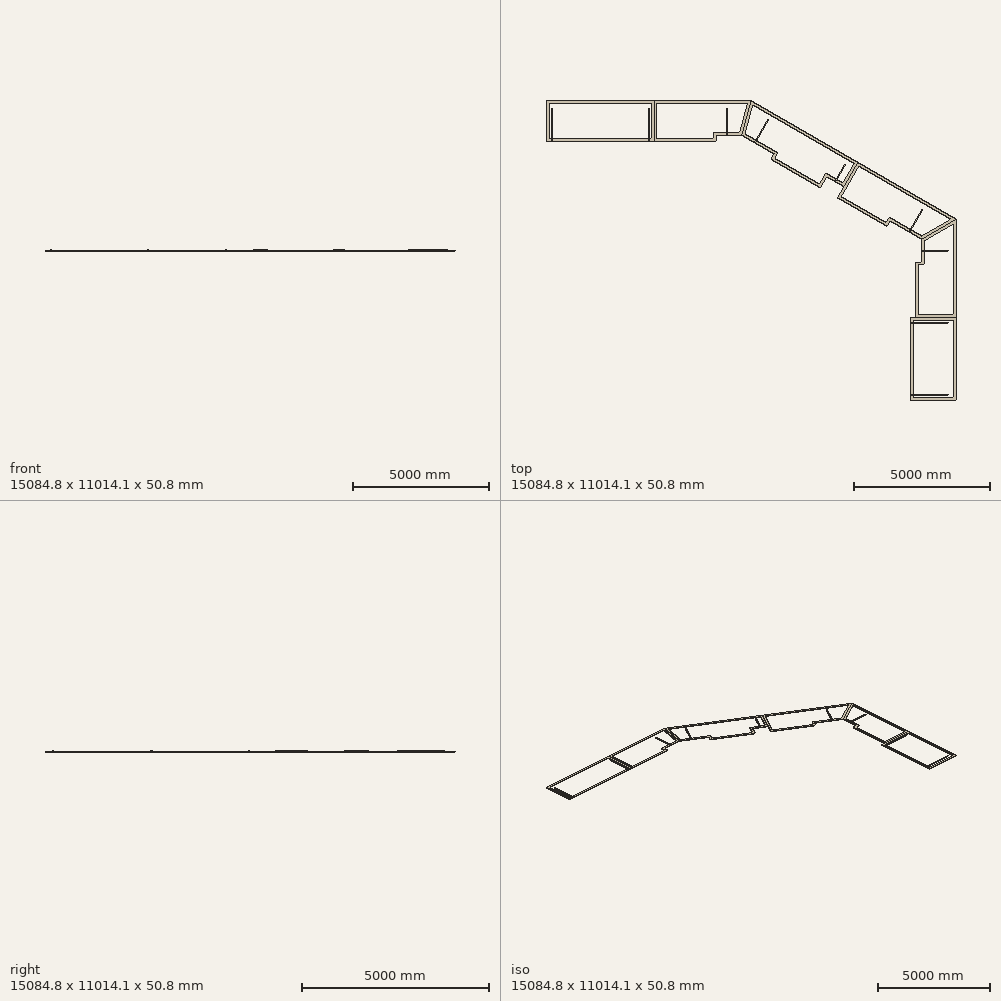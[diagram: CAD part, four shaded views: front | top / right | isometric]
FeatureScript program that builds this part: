
annotation { "Feature Type Name" : "Feature", "Feature Type Description" : "" }
export const myFeature = defineFeature(function(context is Context, id is Id, definition is map)
    precondition{}
    {
        {
            var Q0;
            Q0=qCreatedBy(makeId("Top.planeOp"),FACE);
            var sketch = newSketch(context, id + "F0", { "sketchPlane" : qUnion([Q0])});
            skLineSegment(sketch, "E0", {"start": v(0, 0) * mm, "end": v(7528.5, 0) * mm});
            skLineSegment(sketch, "E1", {"start": v(7528.5, 0) * mm, "end": v(15084.8, -4362.64) * mm});
            skLineSegment(sketch, "E2", {"start": v(15084.8, -4362.64) * mm, "end": v(15084.8, -11014.07) * mm});
            skLineSegment(sketch, "E3", {"start": v(15084.8, -11014.07) * mm, "end": v(13383, -11014.07) * mm});
            skLineSegment(sketch, "E4", {"start": v(13383, -11014.07) * mm, "end": v(13383, -7966.07) * mm});
            skLineSegment(sketch, "E5", {"start": v(13383, -7966.07) * mm, "end": v(13586.2, -7966.07) * mm});
            skLineSegment(sketch, "E6", {"start": v(13586.2, -7966.07) * mm, "end": v(13586.2, -5934.07) * mm});
            skLineSegment(sketch, "E7", {"start": v(13586.2, -5934.07) * mm, "end": v(13814.8, -5934.07) * mm});
            skLineSegment(sketch, "E8", {"start": v(13814.8, -5934.07) * mm, "end": v(13814.8, -5095.87) * mm});
            skLineSegment(sketch, "E9", {"start": v(13814.8, -5095.87) * mm, "end": v(12654.47, -4425.95) * mm});
            skLineSegment(sketch, "E10", {"start": v(12654.47, -4425.95) * mm, "end": v(12540.17, -4623.92) * mm});
            skLineSegment(sketch, "E11", {"start": v(12540.17, -4623.92) * mm, "end": v(10714.41, -3569.82) * mm});
            skLineSegment(sketch, "E12", {"start": v(10714.41, -3569.82) * mm, "end": v(10949.36, -3162.88) * mm});
            skLineSegment(sketch, "E13", {"start": v(10949.36, -3162.88) * mm, "end": v(10322.45, -2800.93) * mm});
            skLineSegment(sketch, "E14", {"start": v(10322.45, -2800.93) * mm, "end": v(10087.5, -3207.87) * mm});
            skLineSegment(sketch, "E15", {"start": v(10087.5, -3207.87) * mm, "end": v(8261.74, -2153.77) * mm});
            skLineSegment(sketch, "E16", {"start": v(8261.74, -2153.77) * mm, "end": v(8376.04, -1955.8) * mm});
            skLineSegment(sketch, "E17", {"start": v(8376.04, -1955.8) * mm, "end": v(7188.2, -1270) * mm});
            skLineSegment(sketch, "E18", {"start": v(7188.2, -1270) * mm, "end": v(6248.4, -1270) * mm});
            skLineSegment(sketch, "E19", {"start": v(6248.4, -1270) * mm, "end": v(6248.4, -1498.6) * mm});
            skLineSegment(sketch, "E20", {"start": v(6248.4, -1498.6) * mm, "end": v(0, -1498.6) * mm});
            skLineSegment(sketch, "E21", {"start": v(0, -1498.6) * mm, "end": v(0, 0) * mm});
            skLineSegment(sketch, "E22", {"start": v(3962.4, 0) * mm, "end": v(3962.4, -1498.6) * mm});
            skLineSegment(sketch, "E23", {"start": v(10949.36, -3162.88) * mm, "end": v(11463.71, -2272) * mm});
            skLineSegment(sketch, "E24", {"start": v(13586.2, -7966.07) * mm, "end": v(15084.8, -7966.07) * mm});
            skLineSegment(sketch, "E25", {"start": v(7188.2, -1270) * mm, "end": v(7528.5, 0) * mm});
            skLineSegment(sketch, "E26", {"start": v(13814.8, -5095.87) * mm, "end": v(15084.8, -4362.64) * mm});
            skLineSegment(sketch, "E27.0", {"start": v(6146.8, -1397) * mm, "end": v(4064, -1397) * mm});
            skLineSegment(sketch, "E27.1", {"start": v(6146.8, -1168.4) * mm, "end": v(6146.8, -1397) * mm});
            skLineSegment(sketch, "E27.2", {"start": v(7110.24, -1168.4) * mm, "end": v(6146.8, -1168.4) * mm});
            skLineSegment(sketch, "E27.3", {"start": v(8514.83, -1918.61) * mm, "end": v(7306.52, -1221) * mm});
            skLineSegment(sketch, "E27.4", {"start": v(8400.53, -2116.59) * mm, "end": v(8514.83, -1918.61) * mm});
            skLineSegment(sketch, "E27.5", {"start": v(101.6, -1397) * mm, "end": v(101.6, -101.6) * mm});
            skLineSegment(sketch, "E27.6", {"start": v(10050.3, -3069.09) * mm, "end": v(8400.53, -2116.59) * mm});
            skLineSegment(sketch, "E27.7", {"start": v(10285.26, -2662.14) * mm, "end": v(10050.3, -3069.09) * mm});
            skLineSegment(sketch, "E27.9", {"start": v(10853.2, -3532.64) * mm, "end": v(11049.76, -3192.19) * mm});
            skLineSegment(sketch, "E27.10", {"start": v(12502.98, -4485.14) * mm, "end": v(10853.2, -3532.64) * mm});
            skLineSegment(sketch, "E27.11", {"start": v(12617.28, -4287.16) * mm, "end": v(12502.98, -4485.14) * mm});
            skLineSegment(sketch, "E27.12", {"start": v(14983.2, -10912.47) * mm, "end": v(13484.6, -10912.47) * mm});
            skLineSegment(sketch, "E27.13", {"start": v(14983.2, -4538.62) * mm, "end": v(14983.2, -7864.47) * mm});
            skLineSegment(sketch, "E27.14", {"start": v(7501.27, -101.6) * mm, "end": v(7501.27, -101.6) * mm});
            skLineSegment(sketch, "E27.15", {"start": v(101.6, -101.6) * mm, "end": v(3860.8, -101.6) * mm});
            skLineSegment(sketch, "E27.16", {"start": v(13484.6, -10912.47) * mm, "end": v(13484.6, -8067.67) * mm});
            skLineSegment(sketch, "E27.17", {"start": v(13484.6, -8067.67) * mm, "end": v(13531.47, -8067.67) * mm});
            skLineSegment(sketch, "E27.19", {"start": v(13687.8, -6035.67) * mm, "end": v(13916.4, -6035.67) * mm});
            skLineSegment(sketch, "E27.20", {"start": v(13916.4, -6035.67) * mm, "end": v(13916.4, -5154.53) * mm});
            skLineSegment(sketch, "E27.21", {"start": v(13814.8, -4978.56) * mm, "end": v(12617.28, -4287.16) * mm});
            skLineSegment(sketch, "E28.0", {"start": v(3860.8, -101.6) * mm, "end": v(3860.8, -1397) * mm});
            skLineSegment(sketch, "E29.0", {"start": v(4064, -101.6) * mm, "end": v(4064, -1397) * mm});
            skLineSegment(sketch, "E30.0", {"start": v(7306.52, -1221) * mm, "end": v(7592.36, -154.2) * mm});
            skLineSegment(sketch, "E31.0", {"start": v(7110.24, -1168.4) * mm, "end": v(7396.09, -101.6) * mm});
            skLineSegment(sketch, "E32.trimOffspring", {"start": v(4064, -101.6) * mm, "end": v(7396.09, -101.6) * mm});
            skLineSegment(sketch, "E33.trimOffspring", {"start": v(3860.8, -1397) * mm, "end": v(101.6, -1397) * mm});
            skLineSegment(sketch, "E34.trimOffspring", {"start": v(7592.36, -154.2) * mm, "end": v(11324.92, -2309.19) * mm});
            skLineSegment(sketch, "E35.trimOffspring", {"start": v(7215.42, -1168.4) * mm, "end": v(7215.42, -1168.4) * mm});
            skLineSegment(sketch, "E36.0", {"start": v(10998.96, -3280.18) * mm, "end": v(11500.9, -2410.79) * mm});
            skLineSegment(sketch, "E37.0", {"start": v(10912.17, -3024.09) * mm, "end": v(11324.92, -2309.19) * mm});
            skLineSegment(sketch, "E38.0", {"start": v(13916.4, -5154.53) * mm, "end": v(14983.2, -4538.62) * mm});
            skLineSegment(sketch, "E39.0", {"start": v(13814.8, -4978.56) * mm, "end": v(14881.6, -4362.64) * mm});
            skLineSegment(sketch, "E40.0", {"start": v(13429.87, -8067.67) * mm, "end": v(14983.2, -8067.67) * mm});
            skLineSegment(sketch, "E41.0", {"start": v(13687.8, -7864.47) * mm, "end": v(14983.2, -7864.47) * mm});
            skLineSegment(sketch, "E42.trimOffspring", {"start": v(10912.17, -3024.09) * mm, "end": v(10285.26, -2662.14) * mm});
            skLineSegment(sketch, "E43.trimOffspring", {"start": v(11500.9, -2410.79) * mm, "end": v(14881.6, -4362.64) * mm});
            skLineSegment(sketch, "E44.trimOffspring", {"start": v(11519.5, -2378.58) * mm, "end": v(11551.7, -2322.8) * mm});
            skLineSegment(sketch, "E45.trimOffspring", {"start": v(13916.4, -5037.22) * mm, "end": v(13916.4, -5037.22) * mm});
            skLineSegment(sketch, "E46.trimOffspring", {"start": v(14983.2, -4421.3) * mm, "end": v(14983.2, -4421.3) * mm});
            skLineSegment(sketch, "E47.trimOffspring", {"start": v(13687.8, -7864.47) * mm, "end": v(13687.8, -6035.67) * mm});
            skLineSegment(sketch, "E48.trimOffspring", {"start": v(14983.2, -8067.67) * mm, "end": v(14983.2, -10912.47) * mm});
            skSolve(sketch);
        }
        {
            var Q0;
            {var subQ1=sQuery(id+"F0.wireOp",EDGE,"E21");Q0=makeQuery(id+"F0.imprint","IMPRINT",FACE,{"disambiguationData":[TD([[makeQuery(id+"F0.imprint","IMPRINT",EDGE,{"derivedFrom":subQ1}),-1.0]])]});}
            extrude(context, id + "F1", {"entities" : qUnion([Q0]), "depth" : 25.4 * mm, "offsetDistance" : 25.4 * mm});
        }
        {
            var Q0;
            {var subQ5=sQuery(id+"F0.wireOp",EDGE,"E18");Q0=makeQuery(id+"F0.imprint","IMPRINT",FACE,{"disambiguationData":[TD([[makeQuery(id+"F0.imprint","IMPRINT",EDGE,{"derivedFrom":subQ5}),-1.0]])]});}
            extrude(context, id + "F2", {"entities" : qUnion([Q0]), "depth" : 25.4 * mm, "offsetDistance" : 25.4 * mm});
        }
        {
            var Q0;
            Q0=makeQuery(id+"F0.imprint","IMPRINT",FACE,{"disambiguationData":[TD([[makeQuery(id+"F0.imprint","IMPRINT",EDGE,{"derivedFrom":sQuery(id+"F0.wireOp",EDGE,"E13")}),-1.0]])]});
            extrude(context, id + "F3", {"entities" : qUnion([Q0]), "depth" : 25.4 * mm, "offsetDistance" : 25.4 * mm});
        }
        {
            var Q0;
            {var subQ3=sQuery(id+"F0.wireOp",EDGE,"E9");Q0=makeQuery(id+"F0.imprint","IMPRINT",FACE,{"disambiguationData":[TD([[makeQuery(id+"F0.imprint","IMPRINT",EDGE,{"derivedFrom":subQ3}),-1.0]])]});}
            extrude(context, id + "F4", {"entities" : qUnion([Q0]), "depth" : 25.4 * mm, "offsetDistance" : 25.4 * mm});
        }
        {
            var Q0;
            Q0=makeQuery(id+"F0.imprint","IMPRINT",FACE,{"disambiguationData":[TD([[makeQuery(id+"F0.imprint","IMPRINT",EDGE,{"derivedFrom":sQuery(id+"F0.wireOp",EDGE,"E6")}),-1.0]])]});
            extrude(context, id + "F5", {"entities" : qUnion([Q0]), "depth" : 25.4 * mm, "offsetDistance" : 25.4 * mm});
        }
        {
            var Q0;
            {var subQ4=sQuery(id+"F0.wireOp",EDGE,"E3");Q0=makeQuery(id+"F0.imprint","IMPRINT",FACE,{"disambiguationData":[TD([[makeQuery(id+"F0.imprint","IMPRINT",EDGE,{"derivedFrom":subQ4}),-1.0]])]});}
            extrude(context, id + "F6", {"entities" : qUnion([Q0]), "depth" : 25.4 * mm, "offsetDistance" : 25.4 * mm});
        }
        {
            var Q0;
            Q0=makeQuery(id+"F1.opExtrude","CAP_FACE",FACE,{"disambiguationData":[OSD([sQuery(id+"F0.wireOp",EDGE,"E0"),sQuery(id+"F0.wireOp",EDGE,"E20"),sQuery(id+"F0.wireOp",EDGE,"E21"),sQuery(id+"F0.wireOp",EDGE,"E22"),sQuery(id+"F0.wireOp",EDGE,"E27.5"),sQuery(id+"F0.wireOp",EDGE,"E27.15"),sQuery(id+"F0.wireOp",EDGE,"E28.0"),sQuery(id+"F0.wireOp",EDGE,"E33.trimOffspring")])],"isStart":false});
            var sketch = newSketch(context, id + "F7", { "sketchPlane" : qUnion([Q0])});
            skLineSegment(sketch, "E49.bottom", {"start": v(184.15, -1498.6) * mm, "end": v(222.25, -1498.6) * mm});
            skLineSegment(sketch, "E49.top", {"start": v(184.15, -304.8) * mm, "end": v(222.25, -304.8) * mm});
            skLineSegment(sketch, "E49.left", {"start": v(184.15, -1498.6) * mm, "end": v(184.15, -304.8) * mm});
            skLineSegment(sketch, "E49.right", {"start": v(222.25, -1498.6) * mm, "end": v(222.25, -304.8) * mm});
            skLineSegment(sketch, "E50.bottom", {"start": v(3752.85, -1498.6) * mm, "end": v(3790.95, -1498.6) * mm});
            skLineSegment(sketch, "E50.top", {"start": v(3752.85, -304.8) * mm, "end": v(3790.95, -304.8) * mm});
            skLineSegment(sketch, "E50.left", {"start": v(3752.85, -1498.6) * mm, "end": v(3752.85, -304.8) * mm});
            skLineSegment(sketch, "E50.right", {"start": v(3790.95, -1498.6) * mm, "end": v(3790.95, -304.8) * mm});
            skLineSegment(sketch, "E51.bottom", {"start": v(6623.05, -1270) * mm, "end": v(6661.15, -1270) * mm});
            skLineSegment(sketch, "E51.top", {"start": v(6623.05, -304.8) * mm, "end": v(6661.15, -304.8) * mm});
            skLineSegment(sketch, "E51.left", {"start": v(6623.05, -1270) * mm, "end": v(6623.05, -304.8) * mm});
            skLineSegment(sketch, "E51.right", {"start": v(6661.15, -1270) * mm, "end": v(6661.15, -304.8) * mm});
            skCircle(sketch, "E52", {"center": v(203.2, -304.8) * mm, "radius": 19.05 * mm});
            skCircle(sketch, "E53", {"center": v(3771.9, -304.8) * mm, "radius": 19.05 * mm});
            skCircle(sketch, "E54", {"center": v(6642.1, -304.8) * mm, "radius": 19.05 * mm});
            skLineSegment(sketch, "E55", {"start": v(7655.64, -1539.88) * mm, "end": v(8138.24, -703.99) * mm});
            skLineSegment(sketch, "E56", {"start": v(8138.24, -703.99) * mm, "end": v(8171.23, -723.04) * mm});
            skLineSegment(sketch, "E57", {"start": v(8171.23, -723.04) * mm, "end": v(7688.63, -1558.92) * mm});
            skLineSegment(sketch, "E58", {"start": v(7688.63, -1558.92) * mm, "end": v(7655.64, -1539.88) * mm});
            skCircle(sketch, "E59", {"center": v(8154.73, -713.51) * mm, "radius": 19.05 * mm});
            skLineSegment(sketch, "E60", {"start": v(10975.86, -2342.29) * mm, "end": v(10613.9, -2969.2) * mm});
            skLineSegment(sketch, "E61", {"start": v(10613.9, -2969.2) * mm, "end": v(10646.9, -2988.25) * mm});
            skLineSegment(sketch, "E62", {"start": v(10646.9, -2988.25) * mm, "end": v(11008.85, -2361.34) * mm});
            skLineSegment(sketch, "E63", {"start": v(11008.85, -2361.34) * mm, "end": v(10975.86, -2342.29) * mm});
            skCircle(sketch, "E64", {"center": v(10992.35, -2351.81) * mm, "radius": 19.05 * mm});
            skLineSegment(sketch, "E65", {"start": v(13824.47, -3986.94) * mm, "end": v(13341.87, -4822.82) * mm});
            skLineSegment(sketch, "E66", {"start": v(13341.87, -4822.82) * mm, "end": v(13374.87, -4841.87) * mm});
            skLineSegment(sketch, "E67", {"start": v(13374.87, -4841.87) * mm, "end": v(13857.47, -4005.99) * mm});
            skLineSegment(sketch, "E68", {"start": v(13857.47, -4005.99) * mm, "end": v(13824.47, -3986.94) * mm});
            skCircle(sketch, "E69", {"center": v(13840.97, -3996.46) * mm, "radius": 19.05 * mm});
            skLineSegment(sketch, "E70.bottom", {"start": v(13814.8, -5521.32) * mm, "end": v(14780, -5521.32) * mm});
            skLineSegment(sketch, "E70.top", {"start": v(13814.8, -5559.42) * mm, "end": v(14780, -5559.42) * mm});
            skLineSegment(sketch, "E70.left", {"start": v(13814.8, -5521.32) * mm, "end": v(13814.8, -5559.42) * mm});
            skLineSegment(sketch, "E70.right", {"start": v(14780, -5521.32) * mm, "end": v(14780, -5559.42) * mm});
            skLineSegment(sketch, "E71.bottom", {"start": v(13383, -8150.22) * mm, "end": v(14780, -8150.22) * mm});
            skLineSegment(sketch, "E71.top", {"start": v(13383, -8188.32) * mm, "end": v(14780, -8188.32) * mm});
            skLineSegment(sketch, "E71.left", {"start": v(13383, -8150.22) * mm, "end": v(13383, -8188.32) * mm});
            skLineSegment(sketch, "E71.right", {"start": v(14780, -8150.22) * mm, "end": v(14780, -8188.32) * mm});
            skLineSegment(sketch, "E72.bottom", {"start": v(13383, -10791.82) * mm, "end": v(14780, -10791.82) * mm});
            skLineSegment(sketch, "E72.top", {"start": v(13383, -10829.92) * mm, "end": v(14780, -10829.92) * mm});
            skLineSegment(sketch, "E72.left", {"start": v(13383, -10791.82) * mm, "end": v(13383, -10829.92) * mm});
            skLineSegment(sketch, "E72.right", {"start": v(14780, -10791.82) * mm, "end": v(14780, -10829.92) * mm});
            skCircle(sketch, "E73", {"center": v(14780, -10810.87) * mm, "radius": 19.05 * mm});
            skCircle(sketch, "E74", {"center": v(14780, -8169.27) * mm, "radius": 19.05 * mm});
            skCircle(sketch, "E75", {"center": v(14780, -5540.37) * mm, "radius": 19.05 * mm});
            skSolve(sketch);
        }
        {
            var Q0;
            Q0 = qSketchRegion(id + "F7", true);
            extrude(context, id + "F8", {"entities" : qUnion([Q0]), "depth" : 25.4 * mm, "offsetDistance" : 25.4 * mm});
        }
    });
